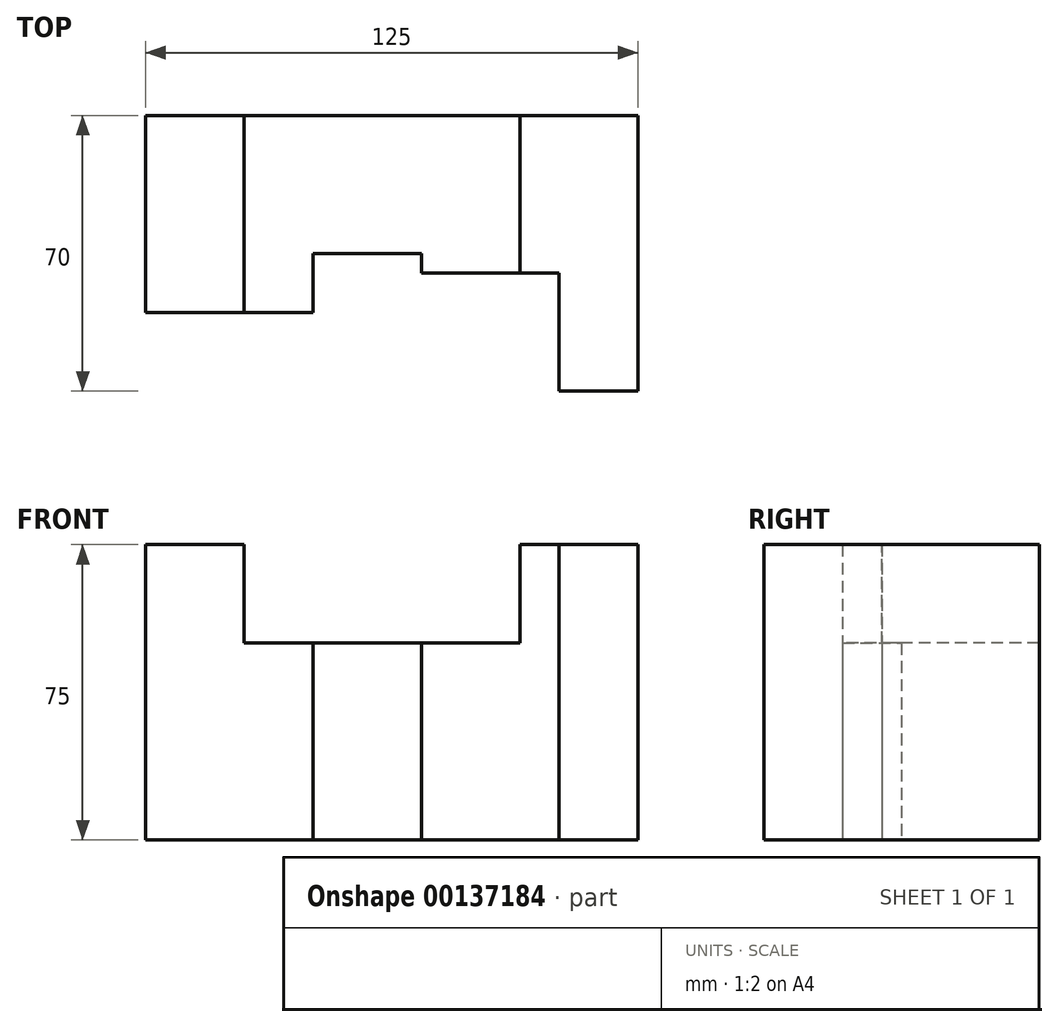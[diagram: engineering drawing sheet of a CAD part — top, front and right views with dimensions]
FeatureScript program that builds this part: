
annotation { "Feature Type Name" : "Feature", "Feature Type Description" : "" }
export const myFeature = defineFeature(function(context is Context, id is Id, definition is map)
    precondition{}
    {
        {
            var Q0;
            Q0=qCreatedBy(makeId("Top.planeOp"),FACE);
            var sketch = newSketch(context, id + "F0", { "sketchPlane" : qUnion([Q0])});
            skLineSegment(sketch, "E0", {"start": v(0, 50) * mm, "end": v(0, 0) * mm});
            skLineSegment(sketch, "E1", {"start": v(0, 0) * mm, "end": v(25, 0) * mm});
            skLineSegment(sketch, "E2", {"start": v(25, 0) * mm, "end": v(25, 50) * mm});
            skLineSegment(sketch, "E3", {"start": v(25, 50) * mm, "end": v(0, 50) * mm});
            skLineSegment(sketch, "E4", {"start": v(25, 50) * mm, "end": v(95, 50) * mm});
            skLineSegment(sketch, "E5", {"start": v(95, 50) * mm, "end": v(95, 10) * mm});
            skLineSegment(sketch, "E6", {"start": v(95, 10) * mm, "end": v(70, 10) * mm});
            skLineSegment(sketch, "E7", {"start": v(70, 10) * mm, "end": v(70, 15) * mm});
            skLineSegment(sketch, "E8", {"start": v(70, 15) * mm, "end": v(42.5, 15) * mm});
            skLineSegment(sketch, "E9", {"start": v(42.5, 15) * mm, "end": v(42.5, 0) * mm});
            skLineSegment(sketch, "E10", {"start": v(42.5, 0) * mm, "end": v(25, 0) * mm});
            skLineSegment(sketch, "E11", {"start": v(95, 10) * mm, "end": v(105, 10) * mm});
            skLineSegment(sketch, "E12", {"start": v(105, 10) * mm, "end": v(105, -20) * mm});
            skLineSegment(sketch, "E13", {"start": v(105, -20) * mm, "end": v(125, -20) * mm});
            skLineSegment(sketch, "E14", {"start": v(125, -20) * mm, "end": v(125, 50) * mm});
            skLineSegment(sketch, "E15", {"start": v(125, 50) * mm, "end": v(95, 50) * mm});
            skSolve(sketch);
        }
        {
            var Q0;
            Q0 = qSketchRegion(id + "F0", true);
            extrude(context, id + "F1", {"entities" : qUnion([Q0]), "depth" : 75 * mm});
        }
        {
            var Q0;
            Q0=qCreatedBy(makeId("Front.planeOp"),FACE);
            var sketch = newSketch(context, id + "F2", { "sketchPlane" : qUnion([Q0])});
            skLineSegment(sketch, "E16.bottom", {"start": v(25, 75) * mm, "end": v(95, 75) * mm});
            skLineSegment(sketch, "E16.top", {"start": v(25, 50) * mm, "end": v(95, 50) * mm});
            skLineSegment(sketch, "E16.left", {"start": v(25, 75) * mm, "end": v(25, 50) * mm});
            skLineSegment(sketch, "E16.right", {"start": v(95, 75) * mm, "end": v(95, 50) * mm});
            skSolve(sketch);
        }
        {
            var Q0;
            Q0 = qSketchRegion(id + "F2", true);
            extrude(context, id + "F3", {"entities" : qUnion([Q0]), "operationType" : NewBodyOperationType.REMOVE, "endBound" : BoundingType.THROUGH_ALL, "oppositeDirection" : true, "depth" : 25 * mm});
        }
    });
